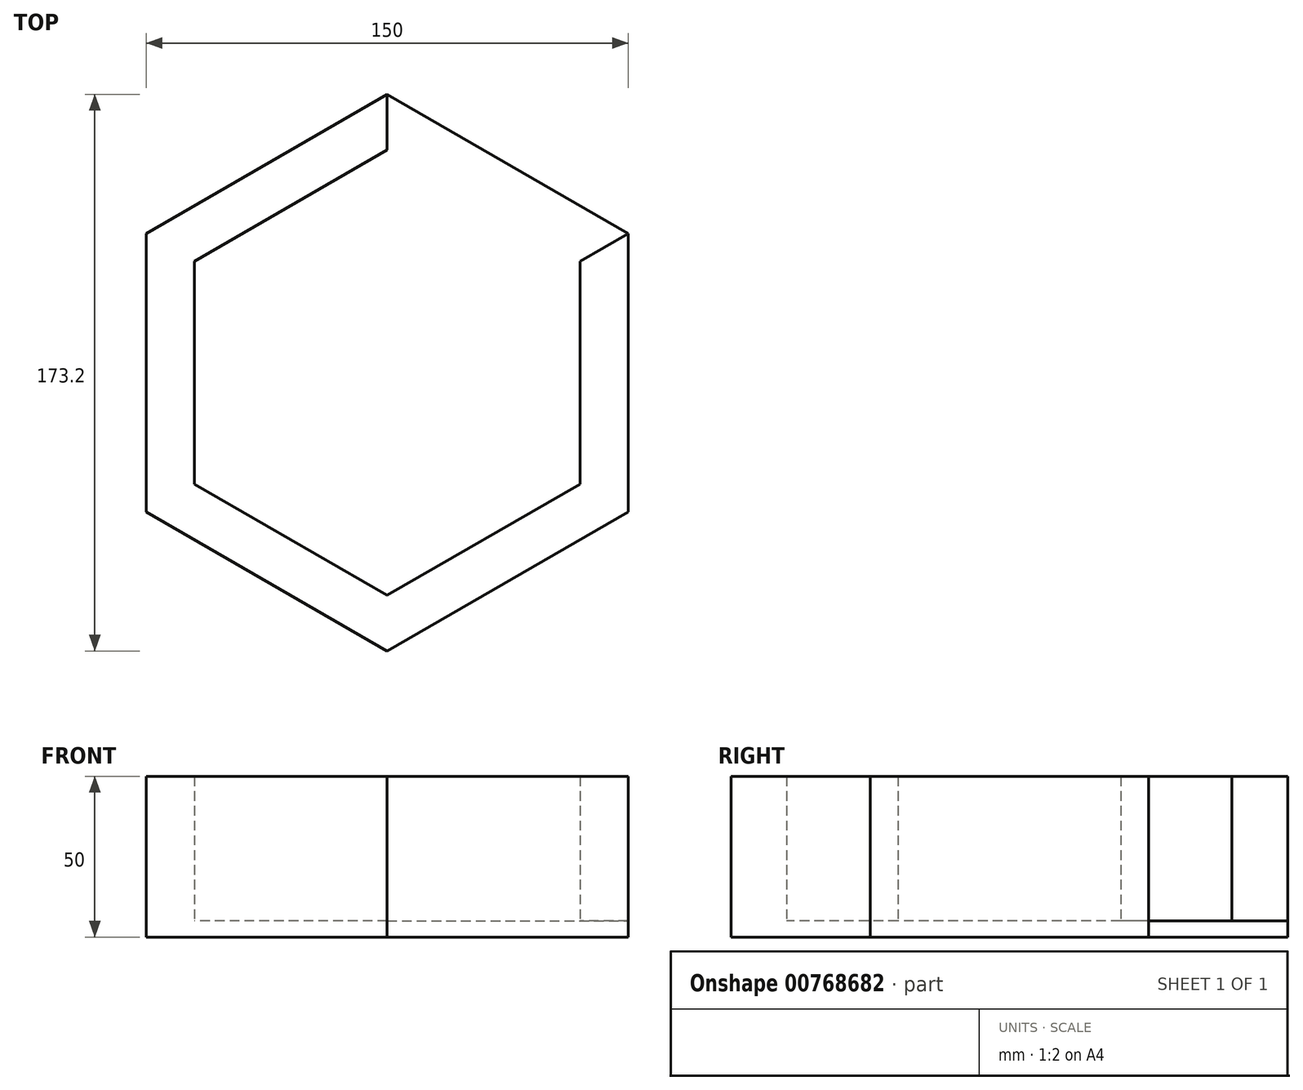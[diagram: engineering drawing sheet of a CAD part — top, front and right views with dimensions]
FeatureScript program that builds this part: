
annotation { "Feature Type Name" : "Feature", "Feature Type Description" : "" }
export const myFeature = defineFeature(function(context is Context, id is Id, definition is map)
    precondition{}
    {
        {
            var Q0;
            Q0=qCreatedBy(makeId("Top.planeOp"),FACE);
            var sketch = newSketch(context, id + "F0", { "sketchPlane" : qUnion([Q0])});
            skCircle(sketch, "E0.cCircle", {"center": v(0, 0) * mm, "radius": 75 * mm, "construction": true});
            skLineSegment(sketch, "E0.0", {"start": v(75, 43.3) * mm, "end": v(75, -43.3) * mm});
            skLineSegment(sketch, "E0.1", {"start": v(75, -43.3) * mm, "end": v(0, -86.6) * mm});
            skLineSegment(sketch, "E0.2", {"start": v(0, -86.6) * mm, "end": v(-75, -43.3) * mm});
            skLineSegment(sketch, "E0.3", {"start": v(-75, -43.3) * mm, "end": v(-75, 43.3) * mm});
            skLineSegment(sketch, "E0.4", {"start": v(-75, 43.3) * mm, "end": v(0, 86.6) * mm});
            skLineSegment(sketch, "E0.5", {"start": v(0, 86.6) * mm, "end": v(75, 43.3) * mm});
            skPoint(sketch, "E0.0.midPoint", {"position": v(75, 0) * mm});
            skCircle(sketch, "E1.cCircle", {"center": v(0, 0) * mm, "radius": 60 * mm, "construction": true});
            skLineSegment(sketch, "E1.0", {"start": v(0, 69.28) * mm, "end": v(60, 34.64) * mm});
            skLineSegment(sketch, "E1.1", {"start": v(60, 34.64) * mm, "end": v(60, -34.64) * mm});
            skLineSegment(sketch, "E1.2", {"start": v(60, -34.64) * mm, "end": v(0, -69.28) * mm});
            skLineSegment(sketch, "E1.3", {"start": v(0, -69.28) * mm, "end": v(-60, -34.64) * mm});
            skLineSegment(sketch, "E1.4", {"start": v(-60, -34.64) * mm, "end": v(-60, 34.64) * mm});
            skLineSegment(sketch, "E1.5", {"start": v(-60, 34.64) * mm, "end": v(0, 69.28) * mm});
            skPoint(sketch, "E1.0.midPoint", {"position": v(30, 51.96) * mm});
            skLineSegment(sketch, "E2", {"start": v(0, 86.6) * mm, "end": v(0, 69.28) * mm});
            skLineSegment(sketch, "E3", {"start": v(60, 34.64) * mm, "end": v(75, 43.3) * mm});
            skLineSegment(sketch, "E4", {"start": v(60, 34.64) * mm, "end": v(108.69, 62.75) * mm});
            skSolve(sketch);
        }
        {
            var Q0;
            Q0 = qSketchRegion(id + "F0", true);
            var Q1;
            Q1=makeQuery(id+"F0.imprint","IMPRINT",FACE,{"disambiguationData":[TD([[makeQuery(id+"F0.imprint","IMPRINT",EDGE,{"derivedFrom":sQuery(id+"F0.wireOp",EDGE,"E1.0")}),-1.0]])]});
            extrude(context, id + "F1", {"entities" : qUnion([Q0, Q1]), "depth" : 5 * mm, "offsetDistance" : 25 * mm});
        }
        {
            var Q0;
            Q0=makeQuery(id+"F0.imprint","IMPRINT",FACE,{"disambiguationData":[TD([[makeQuery(id+"F0.imprint","IMPRINT",EDGE,{"derivedFrom":sQuery(id+"F0.wireOp",EDGE,"E0.0")}),-1.0]])]});
            extrude(context, id + "F2", {"entities" : qUnion([Q0]), "operationType" : NewBodyOperationType.ADD, "depth" : 50 * mm, "offsetDistance" : 25 * mm});
        }
    });
